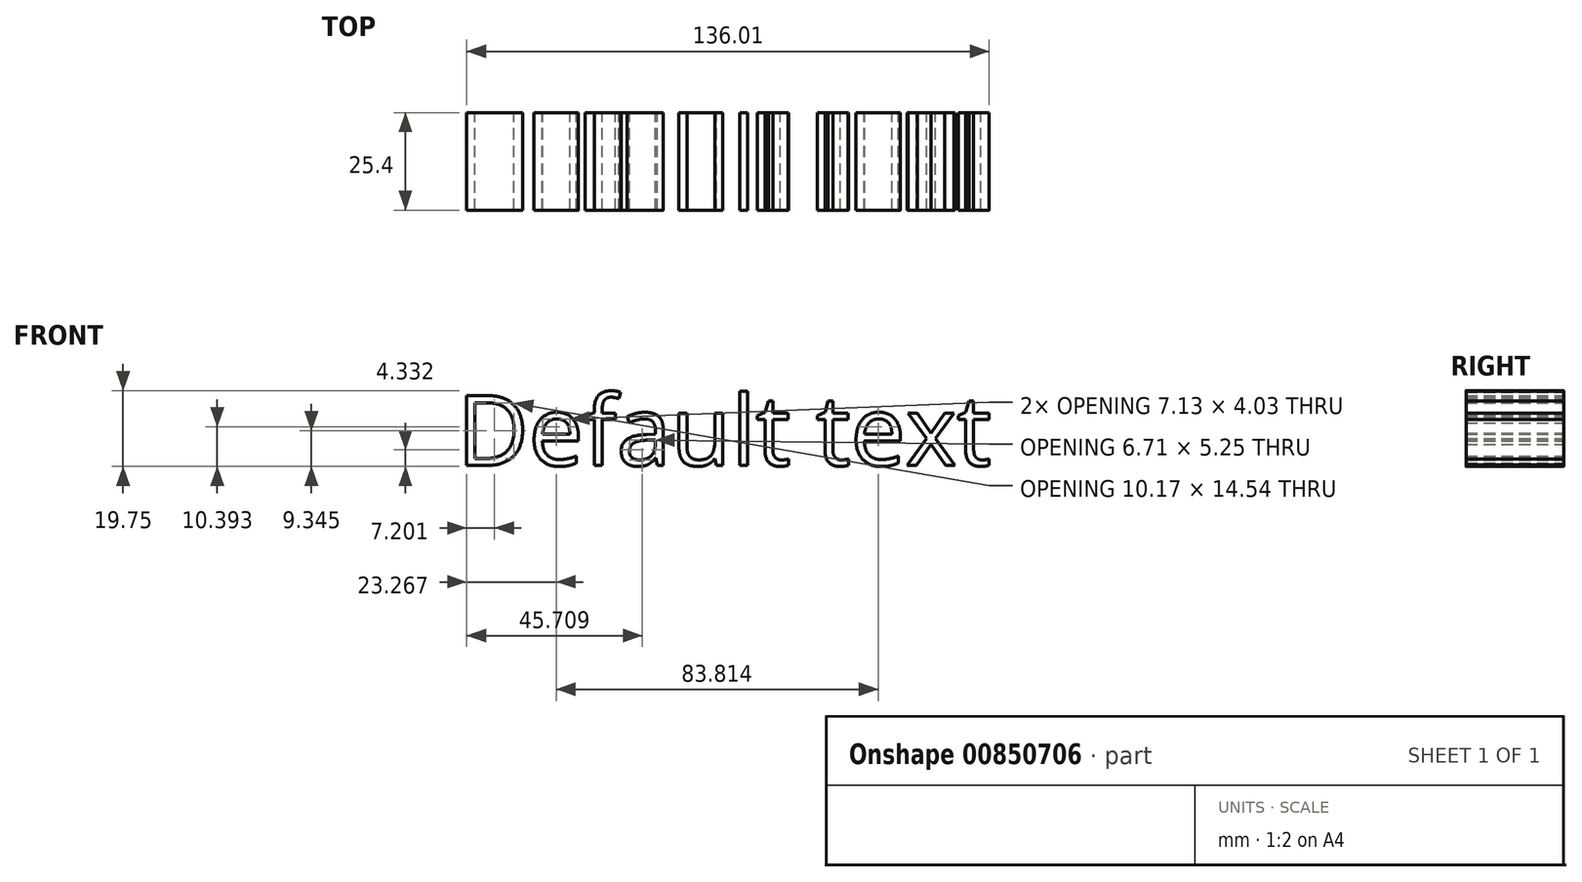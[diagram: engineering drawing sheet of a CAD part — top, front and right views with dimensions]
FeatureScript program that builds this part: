
annotation { "Feature Type Name" : "Feature", "Feature Type Description" : "" }
export const myFeature = defineFeature(function(context is Context, id is Id, definition is map)
    precondition{}
    {
        {
            var Q0;
            Q0=qCreatedBy(makeId("Front.planeOp"),FACE);
            var sketch = newSketch(context, id + "F0", { "sketchPlane" : qUnion([Q0])});
            skText(sketch, "E0", { "text": "Default text", "fontName": "OpenSans-Regular.ttf"});
            const initialGuessF0  = {"E0": [-0.11066, 0.03048, 1, 0, 0.01835]};
            skSetInitialGuess(sketch, initialGuessF0);
            skSolve(sketch);
        }
        {
            var Q0;
            Q0 = qSketchRegion(id + "F0", true);
            extrude(context, id + "F1", {"entities" : qUnion([Q0]), "depth" : 25.4 * mm, "offsetDistance" : 25.4 * mm});
        }
    });
